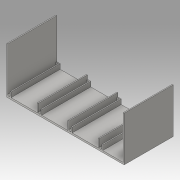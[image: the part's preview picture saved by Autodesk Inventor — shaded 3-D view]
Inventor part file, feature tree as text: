
AUTODESK INVENTOR PART (.ipt)
format: ipt  version: 2016 (Build 200138000, 138)  size: 230,400 bytes
history: native  units: in
note: dims shown in document units (in); Inventor stores cm internally (conversion verified against a paired STEP export)
features: sketch x15, extrude x14, fillet x4
ambient origin geometry x8: Origin, YZ Plane, XZ Plane, XY Plane, X Axis, Y Axis, Z Axis, Center Point
bodies: Solid1 (feature_tree)
feature tree (33):
  extrude  "Extrusion1"  Depth=3.4in TaperAngle=0.0deg
  extrude  "Extrusion2"  Depth=3.1in TaperAngle=0.0deg
  extrude  "Extrusion3"  Depth=0.34in TaperAngle=0.0deg
  extrude  "Extrusion4"  Depth=0.6in TaperAngle=0.0deg
  extrude  "Extrusion5"  Depth=0.34in TaperAngle=0.0deg
  extrude  "Extrusion6"  Depth=0.6in TaperAngle=0.0deg
  extrude  "Extrusion7"  Depth=0.34in TaperAngle=0.0deg
  extrude  "Extrusion8"  Depth=0.6in TaperAngle=0.0deg
  extrude  "Extrusion9"  Depth=0.34in TaperAngle=0.0deg
  sketch  "Sketch14"  dims[d36=0.063in d37=2.982in d38=0.0in]
  extrude  "Extrusion14"  Depth=2.982in TaperAngle=0.0deg
  extrude  "Extrusion15"  Depth=0.063in
  extrude  "Extrusion16"  Depth=0.063in
  extrude  "Extrusion17"  Depth=0.063in
  extrude  "Extrusion18"  Depth=0.09in
  fillet  "Fillet1"  Radius=0.09in
  fillet  "Fillet2"  Radius=0.09in
  fillet  "Fillet3"  Radius=0.09in
  fillet  "Fillet4"  [1 undecoded]
  sketch  "Sketch1"  dims[d0=8.126in d1=3.4in d2=0.0in]
  sketch  "Sketch2"  dims[d3=0.063in d4=3.1in d5=0.0in]
  sketch  "Sketch3"  dims[d6=0.063in d7=0.34in d8=0.0in]
  sketch  "Sketch4"  dims[d9=0.063in d10=0.6in d11=0.0in]
  sketch  "Sketch5"  dims[d12=0.063in d13=0.34in d14=0.0in]
  sketch  "Sketch6"  dims[d15=0.063in d16=0.6in d17=0.0in]
  sketch  "Sketch7"  dims[d18=0.063in d19=0.34in d20=0.0in]
  sketch  "Sketch8"  dims[d21=0.063in d22=0.6in d23=0.0in]
  sketch  "Sketch9"  dims[d24=0.063in d25=0.34in d26=0.0in]
  sketch  "Sketch15"  dims[d39=0.34in d40=0.0in d41=0.063in]
  sketch  "Sketch16"  dims[d42=0.34in d43=0.0in d44=0.063in]
  sketch  "Sketch17"  dims[d45=0.34in d46=0.0in d47=0.063in]
  sketch  "Sketch18"  dims[d48=0.34in d49=0.0in d50=0.09in d51=0.09in d52=0.09in d53=0.09in]
  sketch  "Sketch19"
note: 1 required parameter value undecoded (feature->parameter linkage not recoverable at this tier; creation-order binding heuristic only, values carry confidence <= 0.55)
